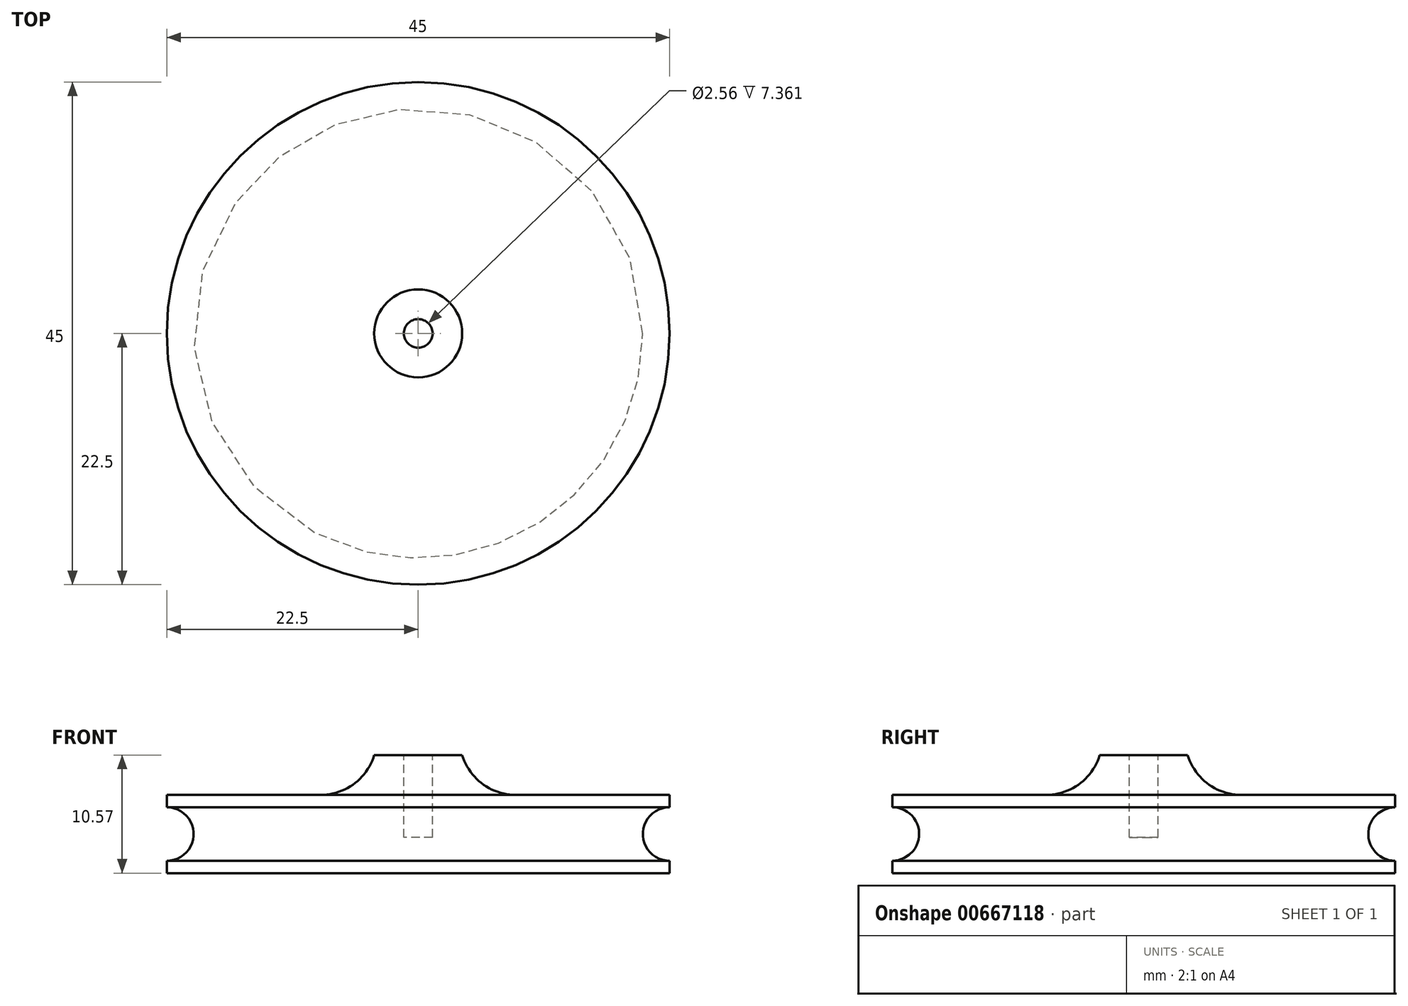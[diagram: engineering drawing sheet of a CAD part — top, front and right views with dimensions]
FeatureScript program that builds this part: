
annotation { "Feature Type Name" : "Feature", "Feature Type Description" : "" }
export const myFeature = defineFeature(function(context is Context, id is Id, definition is map)
    precondition{}
    {
        {
            var Q0;
            Q0=qCreatedBy(makeId("Front.planeOp"),FACE);
            var sketch = newSketch(context, id + "F0", { "sketchPlane" : qUnion([Q0])});
            skLineSegment(sketch, "E0", {"start": v(0, 0) * mm, "end": v(22.5, 0) * mm});
            skLineSegment(sketch, "E1", {"start": v(22.5, 0) * mm, "end": v(22.5, 7) * mm});
            skLineSegment(sketch, "E2", {"start": v(22.5, 7) * mm, "end": v(3.94, 7) * mm});
            skLineSegment(sketch, "E3", {"start": v(3.94, 7) * mm, "end": v(3.94, 10.57) * mm});
            skLineSegment(sketch, "E4", {"start": v(3.94, 10.57) * mm, "end": v(0, 10.57) * mm});
            skLineSegment(sketch, "E5", {"start": v(0, 10.57) * mm, "end": v(0, 0) * mm});
            skLineSegment(sketch, "E6", {"start": v(0, 3.2) * mm, "end": v(1.28, 3.2) * mm});
            skLineSegment(sketch, "E7", {"start": v(1.28, 3.2) * mm, "end": v(1.28, 10.57) * mm});
            skCircle(sketch, "E8", {"center": v(22.5, 3.5) * mm, "radius": 2.4 * mm});
            skSolve(sketch);
        }
        {
            var Q0;
            {var subQ4=sQuery(id+"F0.wireOp",EDGE,"E0");Q0=makeQuery(id+"F0.imprint","IMPRINT",FACE,{"disambiguationData":[TD([[makeQuery(id+"F0.imprint","IMPRINT",EDGE,{"derivedFrom":subQ4}),1.0]])]});}
            var Q1;
            Q1=sQuery(id+"F0.wireOp",EDGE,"E5");
            revolve(context, id + "F1", {"entities" : qUnion([Q0]), "axis" : qUnion([Q1]), "revolveType" : RevolveType.FULL});
        }
        {
            var Q0;
            Q0=makeQuery(id+"F1.opRevolve","SWEPT_EDGE",EDGE,{"disambiguationData":[OSD([sQuery(id+"F0.wireOp",EDGE,"E2"),sQuery(id+"F0.wireOp",EDGE,"E3")])]});
            fillet(context, id + "F2", {"entities" : qUnion([Q0]), "radius" : 5 * mm, "tangentPropagation" : true, "allowEdgeOverflow" : false});
        }
    });
